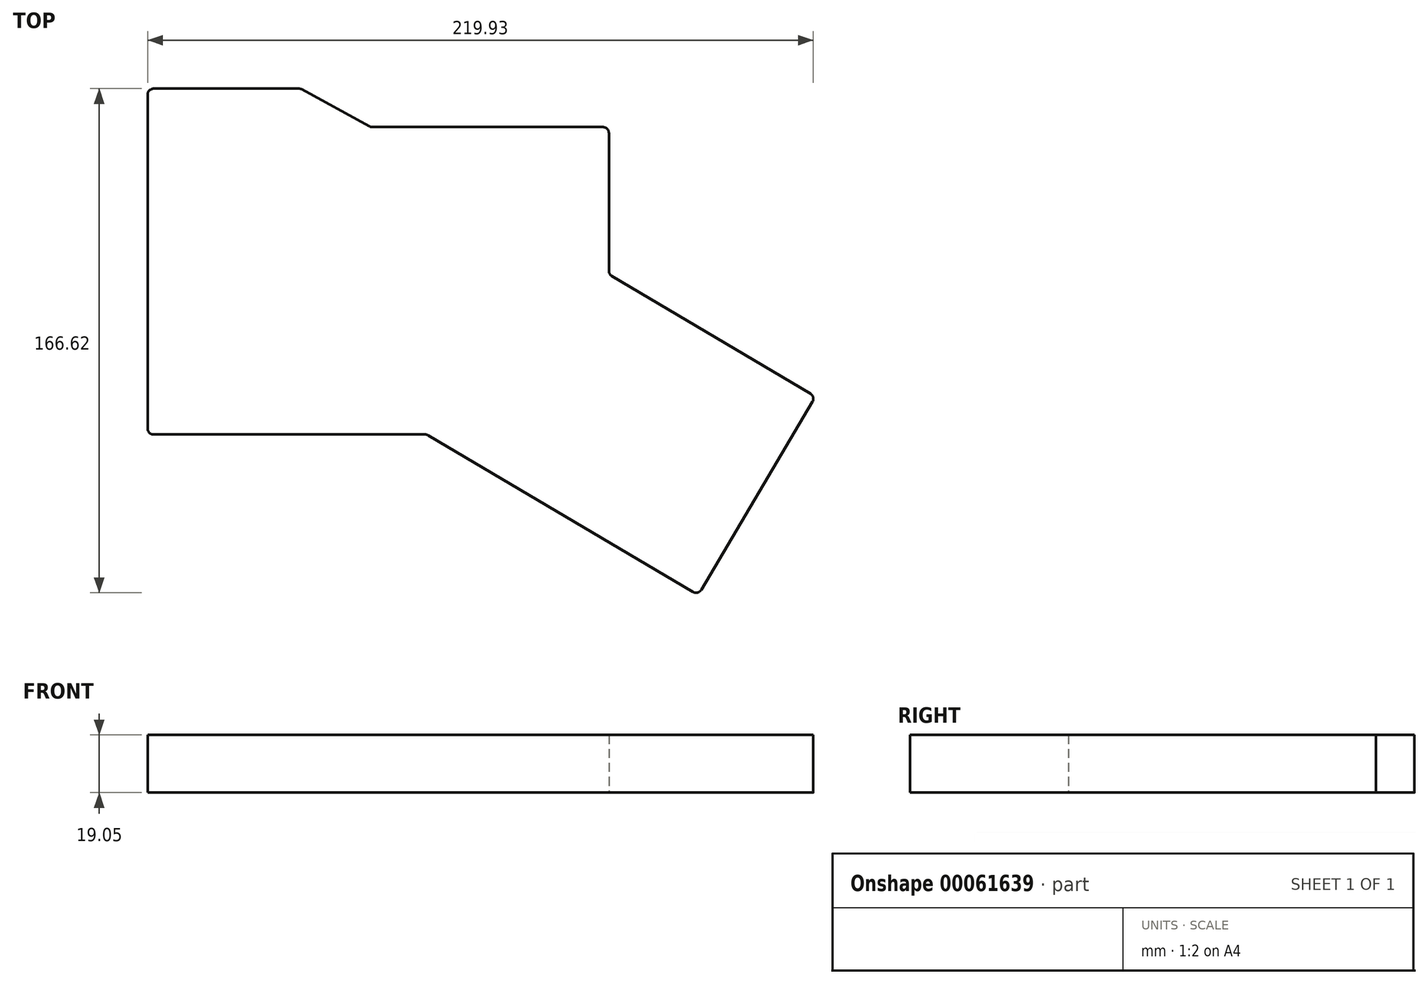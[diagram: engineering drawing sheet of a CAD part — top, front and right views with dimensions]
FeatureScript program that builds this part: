
annotation { "Feature Type Name" : "Feature", "Feature Type Description" : "" }
export const myFeature = defineFeature(function(context is Context, id is Id, definition is map)
    precondition{}
    {
        {
            var Q0;
            Q0=qCreatedBy(makeId("Top.planeOp"),FACE);
            var sketch = newSketch(context, id + "F0", { "sketchPlane" : qUnion([Q0])});
            skLineSegment(sketch, "E0", {"start": v(-102.25, 99.83) * mm, "end": v(-102.25, -10.47) * mm});
            skLineSegment(sketch, "E1", {"start": v(-100.25, -12.47) * mm, "end": v(-10.56, -12.47) * mm});
            skLineSegment(sketch, "E2", {"start": v(-9.55, -12.75) * mm, "end": v(77.88, -64.5) * mm});
            skLineSegment(sketch, "E3", {"start": v(80.62, -63.8) * mm, "end": v(117.4, -1.67) * mm});
            skLineSegment(sketch, "E4", {"start": v(116.7, 1.07) * mm, "end": v(51.13, 39.88) * mm});
            skLineSegment(sketch, "E5", {"start": v(50.15, 41.6) * mm, "end": v(50.15, 87.13) * mm});
            skLineSegment(sketch, "E6", {"start": v(48.15, 89.13) * mm, "end": v(-28.05, 89.13) * mm});
            skLineSegment(sketch, "E7", {"start": v(-29.01, 89.37) * mm, "end": v(-51.29, 101.58) * mm});
            skLineSegment(sketch, "E8", {"start": v(-52.25, 101.83) * mm, "end": v(-100.25, 101.83) * mm});
            skPoint(sketch, "E9.visualSharp", {"position": v(-102.25, 101.83) * mm});
            skArc(sketch, "E9.filletArc", {"start": v(-100.25, 101.83) * mm, "mid": v(-101.67, 101.24) * mm, "end": v(-102.25, 99.83) * mm});
            skPoint(sketch, "E10.visualSharp", {"position": v(-51.74, 101.83) * mm});
            skArc(sketch, "E10.filletArc", {"start": v(-51.29, 101.58) * mm, "mid": v(-51.75, 101.76) * mm, "end": v(-52.25, 101.83) * mm});
            skPoint(sketch, "E11.visualSharp", {"position": v(-28.57, 89.13) * mm});
            skArc(sketch, "E11.filletArc", {"start": v(-29.01, 89.37) * mm, "mid": v(-28.55, 89.19) * mm, "end": v(-28.05, 89.13) * mm});
            skPoint(sketch, "E12.visualSharp", {"position": v(50.15, 89.13) * mm});
            skArc(sketch, "E12.filletArc", {"start": v(50.15, 87.13) * mm, "mid": v(49.56, 88.54) * mm, "end": v(48.15, 89.13) * mm});
            skPoint(sketch, "E13.visualSharp", {"position": v(50.15, 40.46) * mm});
            skArc(sketch, "E13.filletArc", {"start": v(50.15, 41.6) * mm, "mid": v(50.4, 40.61) * mm, "end": v(51.13, 39.88) * mm});
            skPoint(sketch, "E14.visualSharp", {"position": v(118.42, 0.05) * mm});
            skArc(sketch, "E14.filletArc", {"start": v(117.4, -1.67) * mm, "mid": v(117.62, -0.16) * mm, "end": v(116.7, 1.07) * mm});
            skPoint(sketch, "E15.visualSharp", {"position": v(79.6, -65.53) * mm});
            skArc(sketch, "E15.filletArc", {"start": v(77.88, -64.5) * mm, "mid": v(79.4, -64.72) * mm, "end": v(80.62, -63.8) * mm});
            skPoint(sketch, "E16.visualSharp", {"position": v(-10.02, -12.47) * mm});
            skArc(sketch, "E16.filletArc", {"start": v(-9.55, -12.75) * mm, "mid": v(-10.04, -12.54) * mm, "end": v(-10.56, -12.47) * mm});
            skPoint(sketch, "E17.visualSharp", {"position": v(-102.25, -12.47) * mm});
            skArc(sketch, "E17.filletArc", {"start": v(-102.25, -10.47) * mm, "mid": v(-101.67, -11.89) * mm, "end": v(-100.25, -12.47) * mm});
            skSolve(sketch);
        }
        {
            var Q0;
            Q0=makeQuery(id+"F0.imprint","IMPRINT",FACE,{"disambiguationData":[TD([[makeQuery(id+"F0.imprint","IMPRINT",EDGE,{"derivedFrom":sQuery(id+"F0.wireOp",EDGE,"E0")}),1.0]])]});
            extrude(context, id + "F1", {"entities" : qUnion([Q0]), "depth" : 19.05 * mm});
        }
    });
